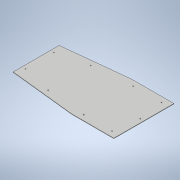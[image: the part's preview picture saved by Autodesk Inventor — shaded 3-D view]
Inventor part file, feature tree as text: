
AUTODESK INVENTOR PART (.ipt)
format: ipt  version: 2021 (Build 250183000, 183)  size: 136,192 bytes
history: native  units: in
note: dims shown in document units (in); Inventor stores cm internally (conversion verified against a paired STEP export)
features: extrude x1, sketch x1
ambient origin geometry x8: Origin, YZ Plane, XZ Plane, XY Plane, X Axis, Y Axis, Z Axis, Center Point
bodies: Solid1 (feature_tree)
feature tree (2):
  extrude  "Extrusion1"  Depth=1.0in
  sketch  "Sketch1"  dims[d0=8.5in d1=12.0in d2=30.5in d3=8.5in d4=12.0in d5=6.5in d6=6.5in d7=0.125in d8=0.0in d9=2.0in d10=1.5in d11=2.0in d12=1.5in d14=1.5in d15=4.0in d16=1.0in d17=4.0in d18=1.0in d19=0.25in d20=0.25in d21=1.5in d22=0.25in d23=2.0in d24=1.5in d25=2.0in d26=1.5in d27=0.25in d28=0.25in d29=0.25in d30=0.25in d31=0.25in d32=1.0in d33=0.25in]
